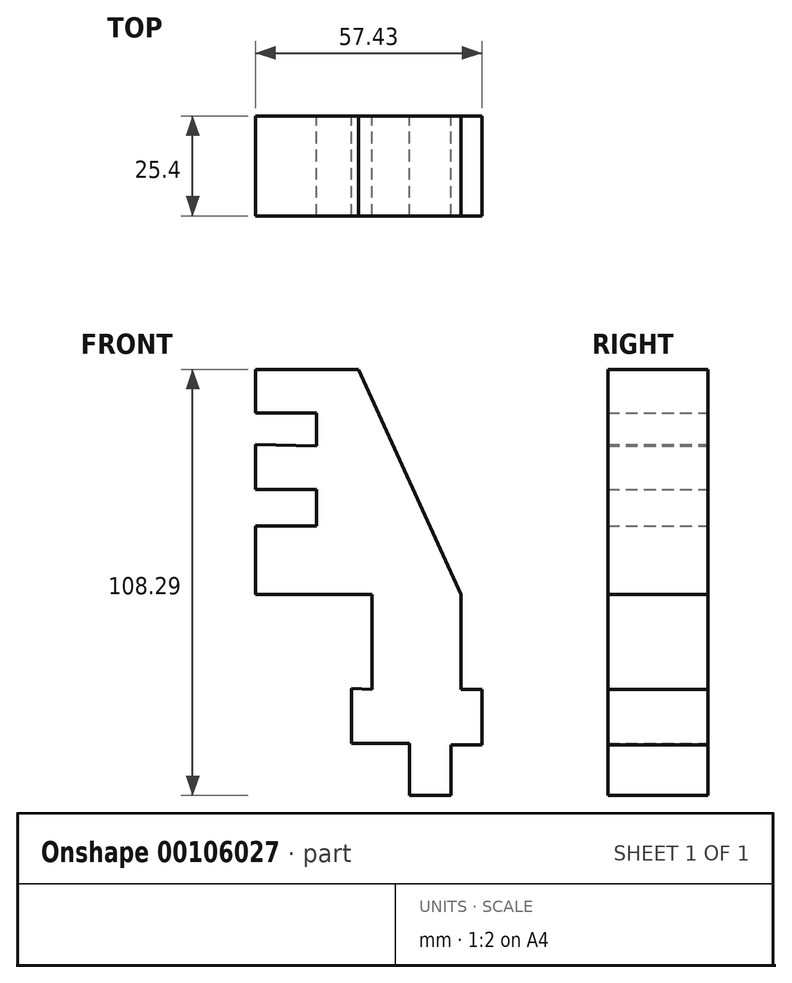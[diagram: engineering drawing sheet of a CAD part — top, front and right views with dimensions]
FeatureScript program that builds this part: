
annotation { "Feature Type Name" : "Feature", "Feature Type Description" : "" }
export const myFeature = defineFeature(function(context is Context, id is Id, definition is map)
    precondition{}
    {
        {
            var Q0;
            Q0=qCreatedBy(makeId("Front.planeOp"),FACE);
            var sketch = newSketch(context, id + "F0", { "sketchPlane" : qUnion([Q0])});
            skLineSegment(sketch, "E0", {"start": v(-15.46, 57.22) * mm, "end": v(10.6, 57.22) * mm});
            skLineSegment(sketch, "E1", {"start": v(10.6, 57.22) * mm, "end": v(36.68, 0) * mm});
            skLineSegment(sketch, "E2", {"start": v(36.68, 0) * mm, "end": v(-15.46, 0) * mm});
            skLineSegment(sketch, "E3", {"start": v(-15.46, 0) * mm, "end": v(-15.46, 17.45) * mm});
            skLineSegment(sketch, "E4", {"start": v(-15.46, 17.45) * mm, "end": v(0, 17.45) * mm});
            skLineSegment(sketch, "E5", {"start": v(0, 17.45) * mm, "end": v(0, 26.73) * mm});
            skLineSegment(sketch, "E6", {"start": v(0, 26.73) * mm, "end": v(-15.46, 26.73) * mm});
            skLineSegment(sketch, "E7", {"start": v(-15.46, 26.73) * mm, "end": v(-15.46, 38.18) * mm});
            skLineSegment(sketch, "E8", {"start": v(-15.46, 38.18) * mm, "end": v(0, 37.77) * mm});
            skLineSegment(sketch, "E9", {"start": v(0, 37.77) * mm, "end": v(0, 46.17) * mm});
            skLineSegment(sketch, "E10", {"start": v(0, 46.17) * mm, "end": v(-15.46, 46.17) * mm});
            skLineSegment(sketch, "E11", {"start": v(-15.46, 46.17) * mm, "end": v(-15.46, 57.22) * mm});
            skLineSegment(sketch, "E12", {"start": v(36.68, 0) * mm, "end": v(36.68, -24.08) * mm});
            skLineSegment(sketch, "E13", {"start": v(36.68, -24.08) * mm, "end": v(14.14, -24.08) * mm});
            skLineSegment(sketch, "E14", {"start": v(14.14, -24.08) * mm, "end": v(14.14, 0) * mm});
            skLineSegment(sketch, "E15", {"start": v(36.68, -24.08) * mm, "end": v(41.97, -24.08) * mm});
            skLineSegment(sketch, "E16", {"start": v(41.97, -24.08) * mm, "end": v(41.97, -38.22) * mm});
            skLineSegment(sketch, "E17", {"start": v(41.97, -38.22) * mm, "end": v(34.11, -38.22) * mm});
            skLineSegment(sketch, "E18", {"start": v(34.11, -38.22) * mm, "end": v(34.11, -51.07) * mm});
            skLineSegment(sketch, "E19", {"start": v(34.11, -51.07) * mm, "end": v(23.57, -51.07) * mm});
            skLineSegment(sketch, "E20", {"start": v(23.57, -51.07) * mm, "end": v(23.57, -37.78) * mm});
            skLineSegment(sketch, "E21", {"start": v(23.57, -37.78) * mm, "end": v(8.84, -37.78) * mm});
            skLineSegment(sketch, "E22", {"start": v(8.84, -37.78) * mm, "end": v(8.84, -23.83) * mm});
            skLineSegment(sketch, "E23", {"start": v(8.84, -23.83) * mm, "end": v(14.14, -24.08) * mm});
            skSolve(sketch);
        }
        {
            var Q0;
            Q0=makeQuery(id+"F0.imprint","IMPRINT",FACE,{"disambiguationData":[TD([[makeQuery(id+"F0.imprint","IMPRINT",EDGE,{"derivedFrom":sQuery(id+"F0.wireOp",EDGE,"E0")}),-1.0]])]});
            var Q1;
            {var subQ0=sQuery(id+"F0.wireOp",EDGE,"E12");Q1=makeQuery(id+"F0.imprint","IMPRINT",FACE,{"disambiguationData":[TD([[makeQuery(id+"F0.imprint","IMPRINT",EDGE,{"derivedFrom":subQ0}),-1.0]])]});}
            var Q2;
            Q2=makeQuery(id+"F0.imprint","IMPRINT",FACE,{"disambiguationData":[TD([[makeQuery(id+"F0.imprint","IMPRINT",EDGE,{"derivedFrom":sQuery(id+"F0.wireOp",EDGE,"E13")}),1.0]])]});
            var Q3;
            Q3=sQuery(id+"F0.wireOp",EDGE,"E13");
            extrude(context, id + "F1", {"entities" : qUnion([Q0, Q1, Q2]), "surfaceEntities" : qUnion([Q3]), "endBound" : BoundingType.SYMMETRIC, "depth" : 25.4 * mm});
        }
    });
